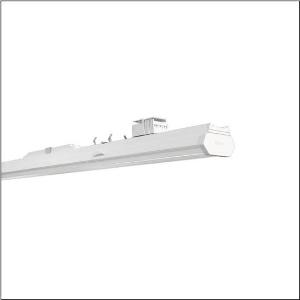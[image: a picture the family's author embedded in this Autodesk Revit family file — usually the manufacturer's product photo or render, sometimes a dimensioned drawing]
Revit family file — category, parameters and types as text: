
# Revit family: licross_r__11_protected_mo_51tp12dn495g_6914
name_source: partatom
category: Lighting Fixtures
units: mm (PartAtom-declared; Revit-internal decimal feet)

## family parameters
Cut with Voids When Loaded = No
Host = Face
Light Source = No
Part Type = Normal
Room Calculation Point = No
Round Connector Dimension = Use Diameter
Shared = No

## types (1)
- --- (1 x LED, 9980 lm, 57.1 W, 4000K)
    Apparent Load = 57 VA
    CIE Flux Codes = 73 92 98 99 100
    Color Rendering = 80
    Color Temperature = 4000K
    Default Elevation = 1800 mm
    Description = Licross® 11 Protected MO, luminaire insert, of sheet steel, galvanised, coil coated, white, length: 1.500mm, width: 90mm, height: 101mm, LED rated luminous flux: 9.980lm, light colour: 840, control gear: DALI 2, with plug, 5-pole, with phase selection, mains connection: 220..240V, AC, 50/60Hz, rated input power: 57W, halogen-free wiring, primary optical cover: cover, of PMMA, light emission: direct distribution, primary light characteristic: symmetric, protection rating (complete): IP64, insulation class (complete): insulation class I (protective earthing), certification: CE, ENEC, VDE, UKCA, protection symbol: D if used in an environment with conductive dust loads with corresponding accessories, impact resistance: IK06, permissible ambient temperature for indoor applications: -25..+35°C, corresponds to IFS (International Featured Standards) requirements for safety and quality in the food industry, reducing of maximum allowable ambient temperature of 5°C with ceiling mounting, LABS conformity tested according to VDMA 24364:2018-05, packaging unit: 1 piece
    Height = 92 mm
    Lamp = 1 x LED
    Lamp Light Flux = 9980 lm
    Lamp Power = 57.1 W
    Lamp count = 1
    Length = 1500 mm
    Luminous efficacy = 175 lm/W
    Manufacturer = Siteco
    ModVariant = No
    Model = 51TP12DN495G
    Mounting Place = Ceiling
    Mounting Type = Pendant
    Number of Poles = 1
    OnlyDefault = Yes
    Power Factor = 1
    Product Name = Licross® 11 Protected MO
    Product group = luminaire insert
    ProductGroupID = 901
    Protection Class = Protection class I
    Protection Degree = IP 64
    RLX_Detail_Level = 1
    RLX_Emergency_Light_Flux = 0 lm
    RLX_Emergency_Type = 0
    RLX_Emergency_Type_DB = No
    RlxData = <blob elided: 24345 chars, md5=fb9d378a>
    Socket = socket
    Standby Power = 0 W
    System Light Flux = 9980 lm
    System Power = 57 W
    Type Comments = factory setting: luminous flux: 100 % | dim-lin: 254 | 378 mA
    Type Image = l_1256148.jpg
    URL = http://relux.com
    VarID = @adj_049383
    Voltage = 0 V
    Weight = 0.00 kg
    Width = 88 mm

## geometry (parser evidence)
native form markers: Blend x4, Sweep x9
no freeform markers — native parametric forms only
